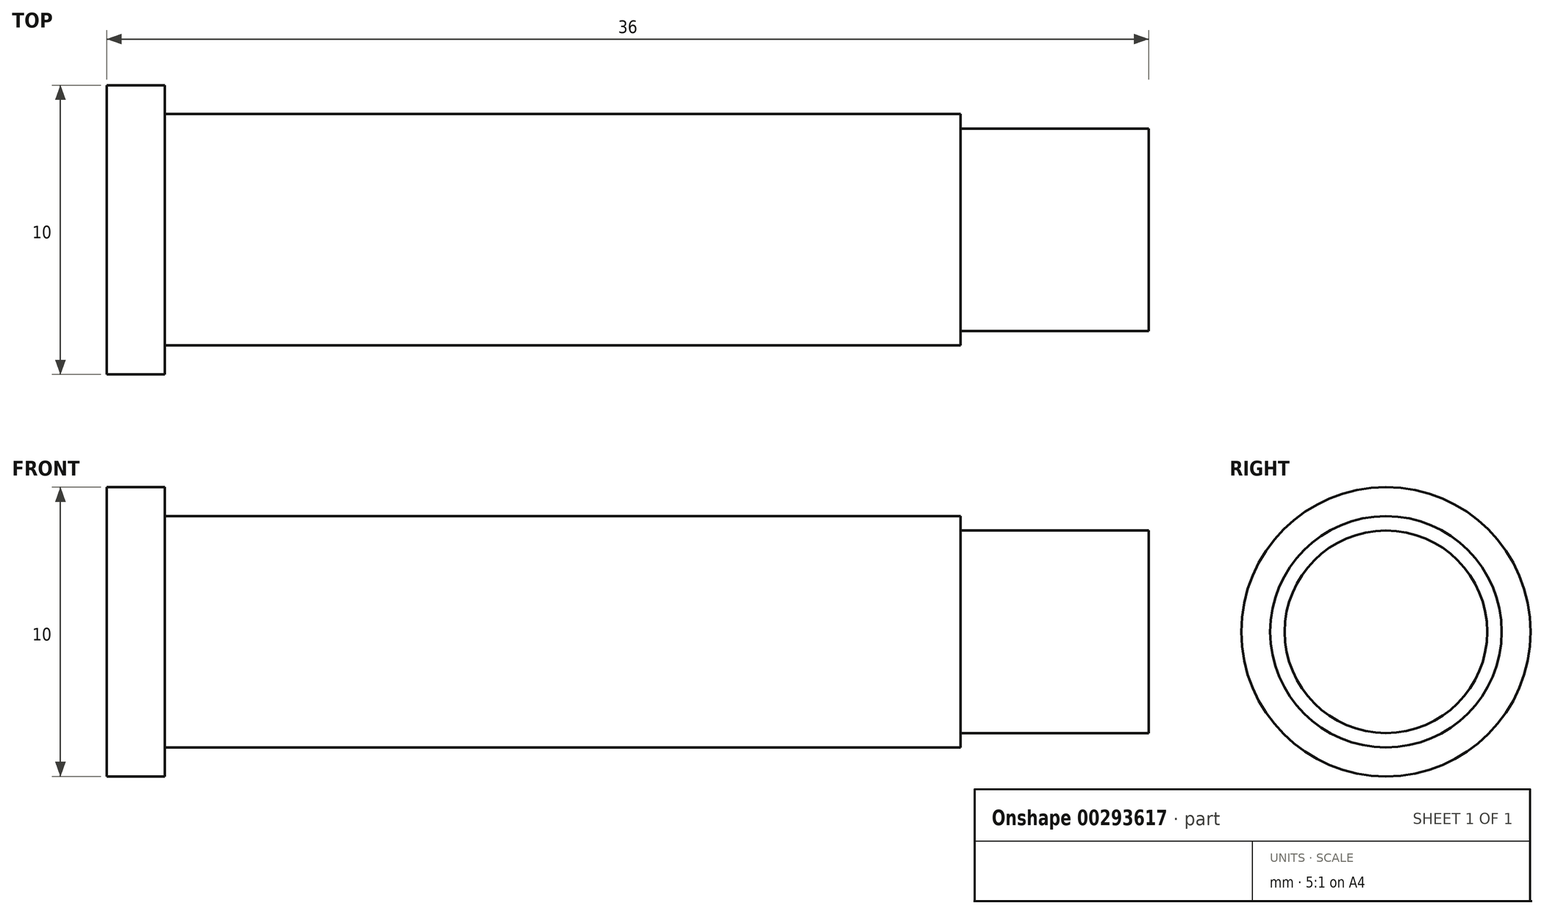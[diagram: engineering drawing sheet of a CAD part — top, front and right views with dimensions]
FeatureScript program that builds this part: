
annotation { "Feature Type Name" : "Feature", "Feature Type Description" : "" }
export const myFeature = defineFeature(function(context is Context, id is Id, definition is map)
    precondition{}
    {
        {
            var Q0;
            Q0=qCreatedBy(makeId("Front.planeOp"),FACE);
            var sketch = newSketch(context, id + "F0", { "sketchPlane" : qUnion([Q0])});
            skLineSegment(sketch, "E0", {"start": v(0, 0) * mm, "end": v(0, 3.5) * mm});
            skLineSegment(sketch, "E1", {"start": v(0, 3.5) * mm, "end": v(-6.5, 3.5) * mm});
            skLineSegment(sketch, "E2", {"start": v(-6.5, 3.5) * mm, "end": v(-6.5, 4) * mm});
            skLineSegment(sketch, "E3", {"start": v(-6.5, 4) * mm, "end": v(-34, 4) * mm});
            skLineSegment(sketch, "E4", {"start": v(-34, 4) * mm, "end": v(-34, 5) * mm});
            skLineSegment(sketch, "E5", {"start": v(-34, 5) * mm, "end": v(-36, 5) * mm});
            skLineSegment(sketch, "E6", {"start": v(-36, 5) * mm, "end": v(-36, 0) * mm});
            skLineSegment(sketch, "E7", {"start": v(-36, 0) * mm, "end": v(0, 0) * mm});
            skSolve(sketch);
        }
        {
            var Q0;
            Q0=makeQuery(id+"F0.imprint","IMPRINT",FACE,{"disambiguationData":[TD([[makeQuery(id+"F0.imprint","IMPRINT",EDGE,{"derivedFrom":sQuery(id+"F0.wireOp",EDGE,"E0")}),1.0]])]});
            var Q1;
            Q1=sQuery(id+"F0.wireOp",EDGE,"E7");
            revolve(context, id + "F1", {"entities" : qUnion([Q0]), "axis" : qUnion([Q1]), "revolveType" : RevolveType.FULL});
        }
    });
